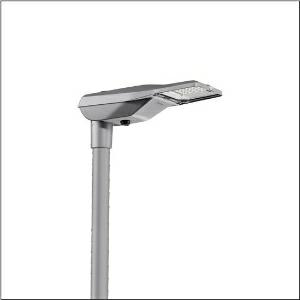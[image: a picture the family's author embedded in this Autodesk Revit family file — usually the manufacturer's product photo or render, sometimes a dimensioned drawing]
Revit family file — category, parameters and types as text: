
# Revit family: streetlight_sl_21_micro___p0_8ab_5xe1r33r08db_894c
name_source: partatom
category: Lighting Fixtures
units: mm (PartAtom-declared; Revit-internal decimal feet)

## family parameters
Cut with Voids When Loaded = No
Host = Face
Light Source = No
Part Type = Normal
Room Calculation Point = No
Round Connector Dimension = Use Diameter
Shared = No

## types (1)
- --- (1 x LED, 4470 lm, 39.1 W, 3000K)
    Apparent Load = 39 VA
    CIE Flux Codes = 36 71 98 100 100
    Color Rendering = 70
    Color Temperature = 3000K
    Default Elevation = 1800 mm
    Description = Streetlight SL 21 micro, mast luminaire, primary light control with lens, of PMMA, primary optical cover: cover, of toughened safety glass, transparent, light distribution: P0.8aB, light emission: direct distribution, primary light characteristic: asymmetric, installation type: post-top, side-entry, LED, High Power LED, rated luminous flux: 4.470lm, luminous efficacy: 114lm/W, light colour: 730, colour temperature: 3000K, control gear: D4i, control: pre-setting: logarithmic dimming characteristic, flexible luminous flux parameterisation, time-dependent luminous flux control, constant luminous flux control, overheat protection, mains connection: 220..240V, AC, 50/60Hz, start of lifetime: 39W, end of service life: 41W, reduction: 18W, luminaire housing, of diecast aluminium, powder-coated, Siteco® metallic grey (DB 702S), corrosivity category C5 mid according to DIN EN ISO 12944, multi-level sealing system, sealing non-destructively replaceable, inclination adjustable: 0°, 5°, 10°, 15°, please order mast flange separately, length: 528mm, width: 235mm, height: 110mm, mast flange for spigot size: 42mm (side-entry): 5XC10008XM4, 60/48mm (side-entry/post-top): 5XC10108XM2, 76/60mm (side-entry/post-top): 5XC10108XM1, Smart Interface below, protection rating (complete): IP66, insulation class (complete): insulation class II (safety insulation), certification: CE, ENEC, ENEC+, VDE, impact resistance: IK09, permissible operating ambient temperature for outdoor applications: -40..+50°C, standard-compliant lighting for roads and squares, packaging unit: 1 piece

Light Distribution: P0.8aB
    Height = 110 mm
    Lamp = 1 x LED
    Lamp Light Flux = 4470 lm
    Lamp Power = 39.1 W
    Lamp count = 1
    Length = 528 mm
    Luminous efficacy = 114 lm/W
    Manufacturer = Siteco
    ModVariant = No
    Model = 5XE1R33R08DB
    Number of Poles = 1
    OnlyDefault = Yes
    Power Factor = 1
    Product Name = Streetlight SL 21 micro | P0.8aB
    Product group = mast luminaire | pylon top
    ProductGroupID = 6100
    Protection Class = Protection class II
    Protection Degree = IP 66
    RLX_Detail_Level = 1
    RLX_Emergency_Light_Flux = 0 lm
    RLX_Emergency_Type = 0
    RLX_Emergency_Type_DB = No
    RlxData = <blob elided: 99277 chars, md5=de0ecfcc>
    Socket = socket
    Standby Power = 0 W
    System Light Flux = 4470 lm
    System Power = 39 W
    Type Comments = factory setting: luminous flux: 100 % | dim-lin: 254 | 765 mA
    Type Image = l_1277290.jpg
    URL = http://relux.com
    VarID = @adj_072308
    Voltage = 0 V
    Weight = 0.00 kg
    Width = 235 mm

## geometry (parser evidence)
native form markers: Blend x4, Sweep x11
no freeform markers — native parametric forms only
